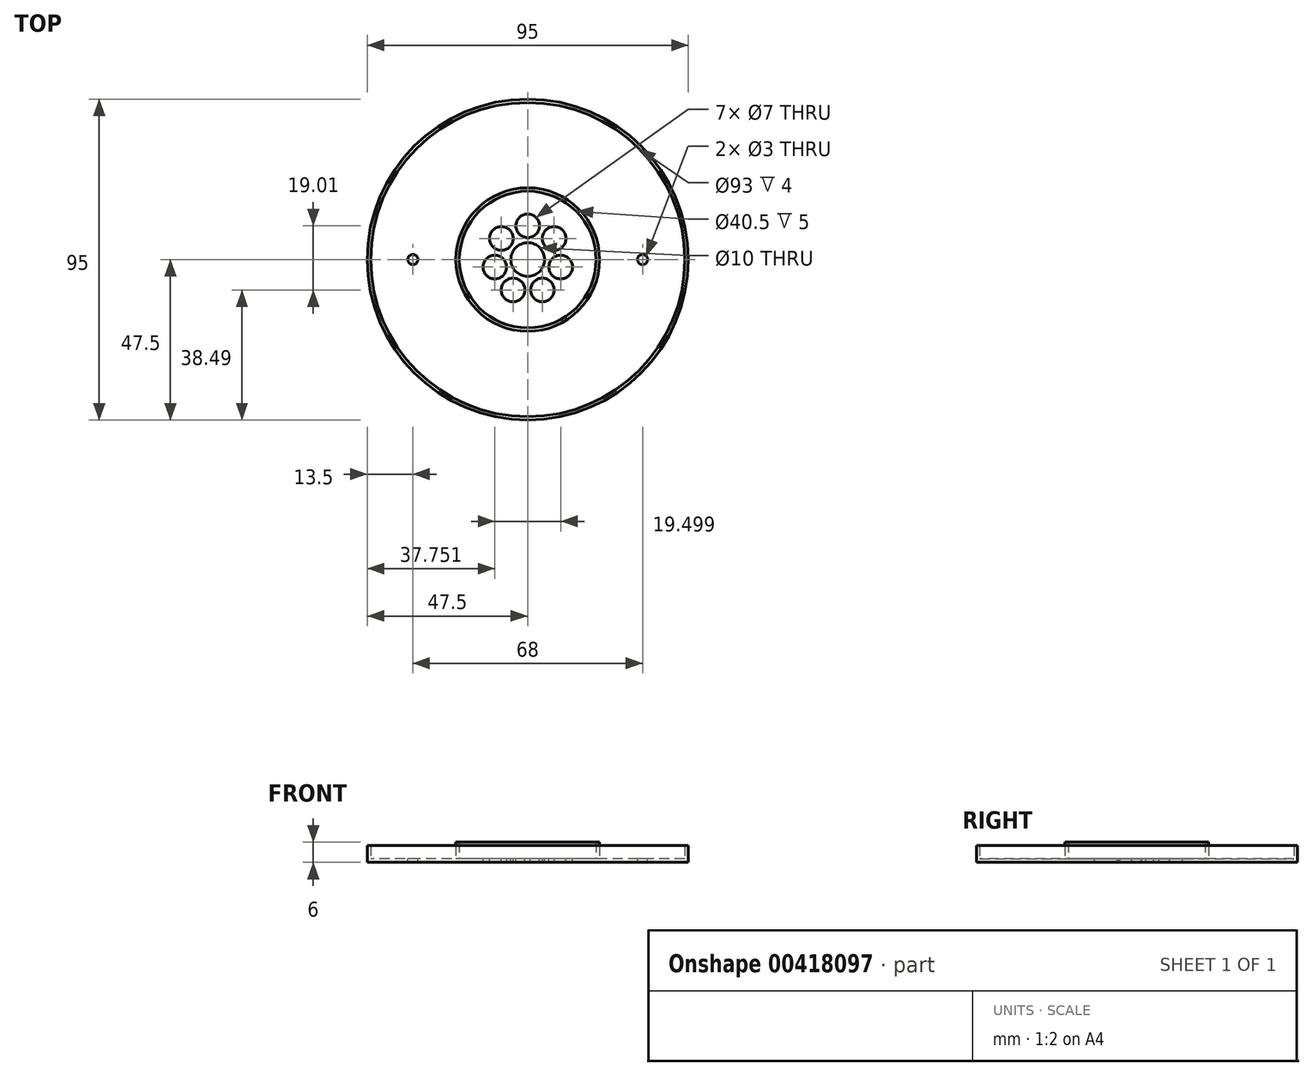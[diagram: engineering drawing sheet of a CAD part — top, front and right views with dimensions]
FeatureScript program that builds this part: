
annotation { "Feature Type Name" : "Feature", "Feature Type Description" : "" }
export const myFeature = defineFeature(function(context is Context, id is Id, definition is map)
    precondition{}
    {
        {
            var Q0;
            Q0=qCreatedBy(makeId("Top.planeOp"),FACE);
            var sketch = newSketch(context, id + "F0", { "sketchPlane" : qUnion([Q0])});
            skCircle(sketch, "E0", {"center": v(0, 0) * mm, "radius": 47.5 * mm});
            skSolve(sketch);
        }
        {
            var Q0;
            Q0=makeQuery(id+"F0.imprint","IMPRINT",FACE,{"disambiguationData":[TD([[makeQuery(id+"F0.imprint","IMPRINT",EDGE,{"derivedFrom":sQuery(id+"F0.wireOp",EDGE,"E0")}),1.0]])]});
            extrude(context, id + "F1", {"entities" : qUnion([Q0]), "depth" : 1 * mm});
        }
        {
            var Q0;
            Q0=makeQuery(id+"F1.opExtrude","CAP_FACE",FACE,{"disambiguationData":[OSD([sQuery(id+"F0.wireOp",EDGE,"E0")])],"isStart":false});
            var sketch = newSketch(context, id + "F2", { "sketchPlane" : qUnion([Q0])});
            skCircle(sketch, "E1", {"center": v(0, 0) * mm, "radius": 47.5 * mm});
            skCircle(sketch, "E2.0", {"center": v(0, 0) * mm, "radius": 46.5 * mm});
            skSolve(sketch);
        }
        {
            var Q0;
            Q0=makeQuery(id+"F2.imprint","IMPRINT",FACE,{"disambiguationData":[TD([[makeQuery(id+"F2.imprint","IMPRINT",EDGE,{"derivedFrom":sQuery(id+"F2.wireOp",EDGE,"E1")}),1.0]])]});
            extrude(context, id + "F3", {"entities" : qUnion([Q0]), "operationType" : NewBodyOperationType.ADD, "depth" : 4 * mm});
        }
        {
            var Q0;
            Q0=makeQuery(id+"F3.boolean.opBoolean","SPLIT",FACE,{"disambiguationData":[TD([makeQuery(id+"F3.opExtrude","SWEPT_FACE",FACE,{"disambiguationData":[OSD([sQuery(id+"F2.wireOp",EDGE,"E2.0")])]})])],"derivedFrom":makeQuery(id+"F1.opExtrude","CAP_FACE",FACE,{"disambiguationData":[OSD([sQuery(id+"F0.wireOp",EDGE,"E0")])],"isStart":false})});
            var sketch = newSketch(context, id + "F4", { "sketchPlane" : qUnion([Q0])});
            skCircle(sketch, "E3", {"center": v(0, 0) * mm, "radius": 20.25 * mm});
            skCircle(sketch, "E4.0", {"center": v(0, 0) * mm, "radius": 21.25 * mm});
            skSolve(sketch);
        }
        {
            var Q0;
            Q0=qSketchRegion(id+"F4",true);
            extrude(context, id + "F5", {"entities" : qUnion([Q0]), "operationType" : NewBodyOperationType.ADD, "depth" : 5 * mm});
        }
        {
            var Q0;
            Q0=makeQuery(id+"F5.boolean.opBoolean","SPLIT",FACE,{"disambiguationData":[TD([makeQuery(id+"F5.opExtrude","SWEPT_FACE",FACE,{"disambiguationData":[OSD([sQuery(id+"F4.wireOp",EDGE,"E3")])]})])],"derivedFrom":makeQuery(id+"F3.boolean.opBoolean","SPLIT",FACE,{"disambiguationData":[TD([makeQuery(id+"F3.opExtrude","SWEPT_FACE",FACE,{"disambiguationData":[OSD([sQuery(id+"F2.wireOp",EDGE,"E2.0")])]})])],"derivedFrom":makeQuery(id+"F1.opExtrude","CAP_FACE",FACE,{"disambiguationData":[OSD([sQuery(id+"F0.wireOp",EDGE,"E0")])],"isStart":false})})});
            var sketch = newSketch(context, id + "F6", { "sketchPlane" : qUnion([Q0])});
            skCircle(sketch, "E5", {"center": v(0, 0) * mm, "radius": 5 * mm});
            skCircle(sketch, "E6", {"center": v(0, 10) * mm, "radius": 3.5 * mm});
            skCircle(sketch, "E7.1.0", {"center": v(-7.82, 6.23) * mm, "radius": 3.5 * mm});
            skCircle(sketch, "E7.2.0", {"center": v(-9.75, -2.23) * mm, "radius": 3.5 * mm});
            skCircle(sketch, "E7.3.0", {"center": v(-4.34, -9) * mm, "radius": 3.5 * mm});
            skCircle(sketch, "E7.4.0", {"center": v(4.34, -9) * mm, "radius": 3.5 * mm});
            skCircle(sketch, "E7.5.0", {"center": v(9.75, -2.23) * mm, "radius": 3.5 * mm});
            skCircle(sketch, "E7.6.0", {"center": v(7.82, 6.23) * mm, "radius": 3.5 * mm});
            skSolve(sketch);
        }
        {
            var Q0;
            Q0=makeQuery(id+"F6.imprint","IMPRINT",FACE,{"disambiguationData":[TD([[makeQuery(id+"F6.imprint","IMPRINT",EDGE,{"derivedFrom":sQuery(id+"F6.wireOp",EDGE,"E7.1.0")}),1.0]])]});
            var Q1;
            Q1=makeQuery(id+"F6.imprint","IMPRINT",FACE,{"disambiguationData":[TD([[makeQuery(id+"F6.imprint","IMPRINT",EDGE,{"derivedFrom":sQuery(id+"F6.wireOp",EDGE,"E7.2.0")}),1.0]])]});
            var Q2;
            Q2=makeQuery(id+"F6.imprint","IMPRINT",FACE,{"disambiguationData":[TD([[makeQuery(id+"F6.imprint","IMPRINT",EDGE,{"derivedFrom":sQuery(id+"F6.wireOp",EDGE,"E7.3.0")}),1.0]])]});
            var Q3;
            Q3=makeQuery(id+"F6.imprint","IMPRINT",FACE,{"disambiguationData":[TD([[makeQuery(id+"F6.imprint","IMPRINT",EDGE,{"derivedFrom":sQuery(id+"F6.wireOp",EDGE,"E7.4.0")}),1.0]])]});
            var Q4;
            Q4=makeQuery(id+"F6.imprint","IMPRINT",FACE,{"disambiguationData":[TD([[makeQuery(id+"F6.imprint","IMPRINT",EDGE,{"derivedFrom":sQuery(id+"F6.wireOp",EDGE,"E7.5.0")}),1.0]])]});
            var Q5;
            Q5=makeQuery(id+"F6.imprint","IMPRINT",FACE,{"disambiguationData":[TD([[makeQuery(id+"F6.imprint","IMPRINT",EDGE,{"derivedFrom":sQuery(id+"F6.wireOp",EDGE,"E7.6.0")}),1.0]])]});
            var Q6;
            Q6=makeQuery(id+"F6.imprint","IMPRINT",FACE,{"disambiguationData":[TD([[makeQuery(id+"F6.imprint","IMPRINT",EDGE,{"derivedFrom":sQuery(id+"F6.wireOp",EDGE,"E6")}),1.0]])]});
            var Q7;
            Q7=makeQuery(id+"F6.imprint","IMPRINT",FACE,{"disambiguationData":[TD([[makeQuery(id+"F6.imprint","IMPRINT",EDGE,{"derivedFrom":sQuery(id+"F6.wireOp",EDGE,"E5")}),1.0]])]});
            extrude(context, id + "F7", {"entities" : qUnion([Q0, Q1, Q2, Q3, Q4, Q5, Q6, Q7]), "operationType" : NewBodyOperationType.REMOVE, "oppositeDirection" : true, "depth" : 25 * mm});
        }
        {
            var Q0;
            {var subQ0=makeQuery(id+"F3.opExtrude","SWEPT_FACE",FACE,{"disambiguationData":[OSD([sQuery(id+"F2.wireOp",EDGE,"E2.0")])]});Q0=makeQuery(id+"F5.boolean.opBoolean","SPLIT",FACE,{"disambiguationData":[TD([subQ0])],"derivedFrom":makeQuery(id+"F3.boolean.opBoolean","SPLIT",FACE,{"disambiguationData":[TD([subQ0])],"derivedFrom":makeQuery(id+"F1.opExtrude","CAP_FACE",FACE,{"disambiguationData":[OSD([sQuery(id+"F0.wireOp",EDGE,"E0")])],"isStart":false})})});}
            var sketch = newSketch(context, id + "F8", { "sketchPlane" : qUnion([Q0])});
            skCircle(sketch, "E8", {"center": v(-34, 0) * mm, "radius": 1.5 * mm});
            skCircle(sketch, "E9", {"center": v(34, 0) * mm, "radius": 1.5 * mm});
            skSolve(sketch);
        }
        {
            var Q0;
            Q0=qSketchRegion(id+"F8",true);
            extrude(context, id + "F9", {"entities" : qUnion([Q0]), "operationType" : NewBodyOperationType.REMOVE, "oppositeDirection" : true, "depth" : 25 * mm});
        }
        {
            var Q0;
            Q0=makeQuery(id+"F1.opExtrude","SWEPT_BODY",BODY,{"disambiguationData":[OSD([sQuery(id+"F0.wireOp",EDGE,"E0")])]});
            transform(context, id + "F10", {"entities" : qUnion([Q0]), "transformType" : TransformType.TRANSLATION_3D, "dx" : 0 * mm, "dy" : 0 * mm, "dz" : 0 * mm, "makeCopy" : true});
        }
        {
            var Q0;
            Q0=makeQuery(id+"F10.opPattern","COPY",BODY,{"derivedFrom":makeQuery(id+"F1.opExtrude","SWEPT_BODY",BODY,{"disambiguationData":[OSD([sQuery(id+"F0.wireOp",EDGE,"E0")])]}),"instanceName":"1"});
            deleteBodies(context, id + "F11", {"entities" : qUnion([Q0])});
        }
    });
